# Revit family: Lighting-Industrial-GEWISS-SMART[3]PLUS-WATERTIGHT-LED_TRANSPARENT_1200mm
name_source: partatom
category: Apparecchi per illuminazione
units: mm (PartAtom-declared; Revit-internal decimal feet)

## family parameters
Condiviso = No
Host = Superficie
Punto di calcolo locali = No
Quota connettore circolare = Usa diametro
Sorgente d'illuminazione = Sì
Taglio con vuoti quando caricato = No
Tipo di parte = Normale

## types (1)
- Lighting-Industrial-GEWISS-SMART[3]PLUS-WATERTIGHT-LED_TRANSPARENT_1200mm
    Angolo inclinazione = -90.00°
    Application = Indoor
    Carico apparente = 20 VA
    Catalogue = LIGHTING
    Catalogue Range = SMART[3] PLUS
    Colour temperature = 5700 K (CRI > 90)
    Colour temperature: = 5700 K (CRI > 90)
    Commenti sul wattaggio = 20W
    Descrizione = SMART3 PLUS 1200 T.W.DALI HE TRASP 9 57
    Efficiency class of integrated LEDs = A ÷ A++
    Electrocod = 2434
    Emetti da lunghezza linea = 1000 mm  [stored 3.28084 ft]
    File diagramma fotometrico = GWS3223AT957.IES
    Filtro dei colori = 16777215
    Ganci = GEWISS  - ALLUMINIO
    Glow Wire Test = 850°C
    IDF = 927492b9-7e84-4dff-8bc6-ba5daba70ad1
    IDT = c46b9b55-ed1d-4068-afb8-069052944d3c
    IP degree = IP66/IP69
    Immagine tipo = GWS3136T.jpg
    Insulation class = II
    Lamp = LED
    Lampada = LED
    Length = 1200 mm
    Lumen output (lm) = 4500
    Lunghezza Lampada = 1200 mm
    Modello = GWS3223AT957
    Operating temperature: = -25 +50 °C
    Produttore = GEWISS S.p.A.
    Prospetto di default = 1219 mm
    SEO = Ceiling
    Schermo. = Gewiss - Led Acceso
    Shield type = Transparent
    Shock resistance = IK08
    Stampa 1_100 = Sì
    Stampa 1_200 = No
    Struttura = GEWISS - SMART 3 - GRIGIO
    System power = 38 W
    Technical sheet = https://www.gewiss.com
    Type of light source = LED - Not replaceable
    Typology = DALI
    URL = https://www.gewiss.com
    Variazione temperatura colore lampada con luminosità attenuata = <Nessuno>
    Version file RFA = 20.0
    Voltage = 220-240 V
    Warranty = 5 years
    Working temperature = -25 +50 °C

note: [stored X ft] marks values corroborated as IEEE doubles in the binary element streams (Revit-internal decimal feet)
